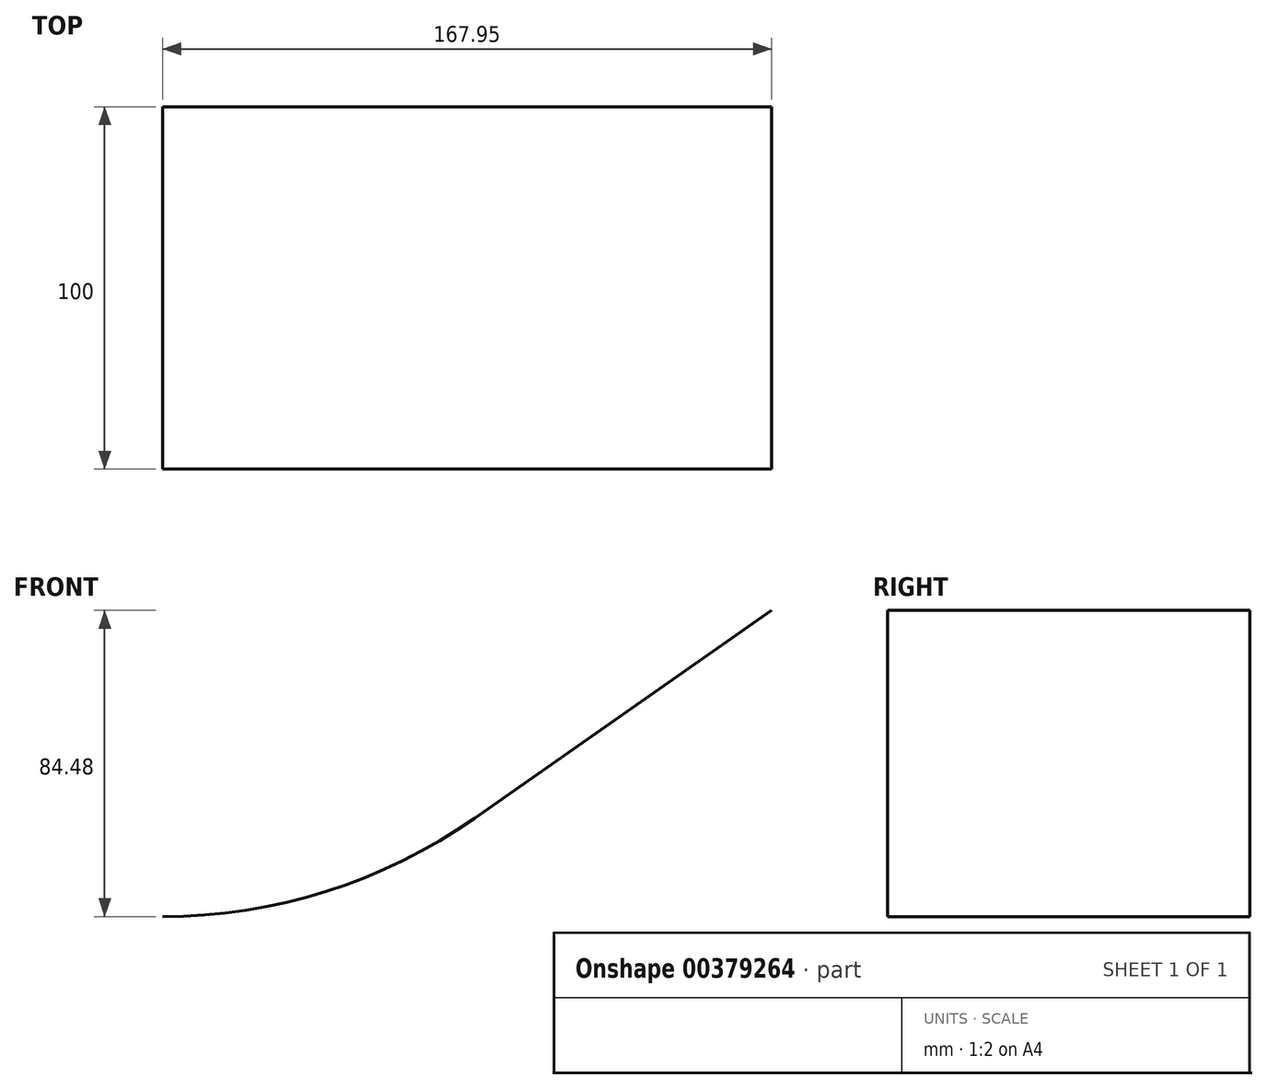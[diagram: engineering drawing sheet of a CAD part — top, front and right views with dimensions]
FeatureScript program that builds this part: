
annotation { "Feature Type Name" : "Feature", "Feature Type Description" : "" }
export const myFeature = defineFeature(function(context is Context, id is Id, definition is map)
    precondition{}
    {
        {
            var Q0;
            Q0=qCreatedBy(makeId("Front.planeOp"),FACE);
            var sketch = newSketch(context, id + "F0", { "sketchPlane" : qUnion([Q0])});
            skArc(sketch, "E0", {"start": v(0, 0) * mm, "mid": v(45.1, 6.94) * mm, "end": v(86.04, 27.13) * mm});
            skLineSegment(sketch, "E1", {"start": v(0, 150) * mm, "end": v(86.04, 27.13) * mm, "construction": true});
            skLineSegment(sketch, "E2", {"start": v(86.04, 27.13) * mm, "end": v(167.95, 84.48) * mm});
            skSolve(sketch);
        }
        {
            var Q0;
            Q0=sQuery(id+"F0.wireOp",EDGE,"E2");
            var Q1;
            Q1=sQuery(id+"F0.wireOp",EDGE,"E0");
            extrude(context, id + "F1", {"bodyType" : ToolBodyType.SURFACE, "surfaceEntities" : qUnion([Q0, Q1]), "endBound" : BoundingType.SYMMETRIC, "depth" : 100 * mm});
        }
    });
